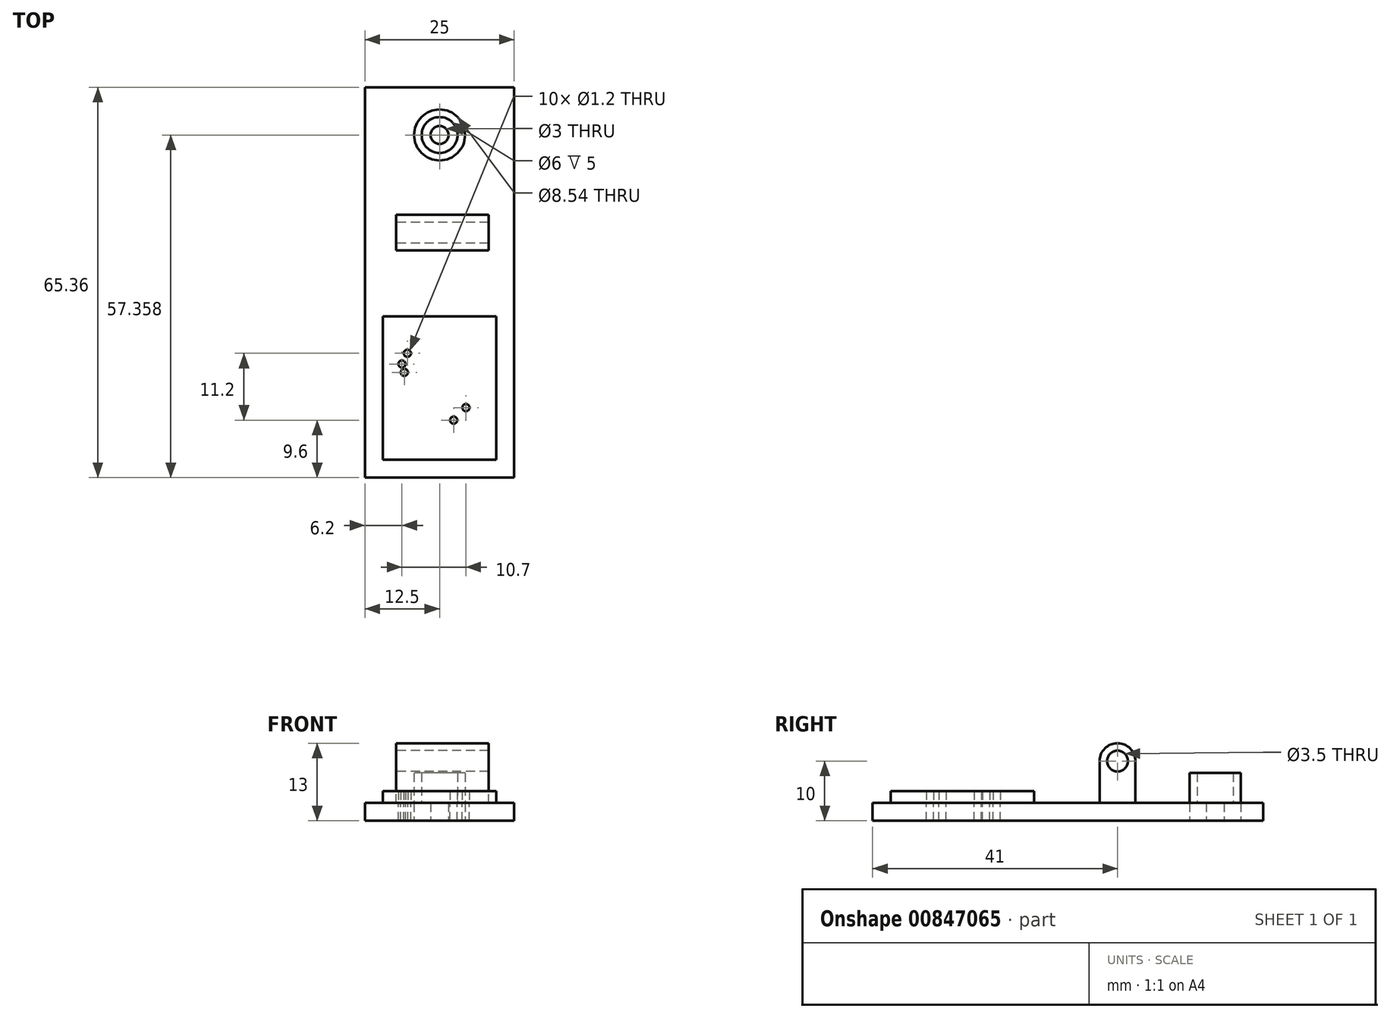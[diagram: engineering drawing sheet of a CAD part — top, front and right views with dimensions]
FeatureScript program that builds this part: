
annotation { "Feature Type Name" : "Feature", "Feature Type Description" : "" }
export const myFeature = defineFeature(function(context is Context, id is Id, definition is map)
    precondition{}
    {
        {
            var Q0;
            Q0=qCreatedBy(makeId("Top.planeOp"),FACE);
            var sketch = newSketch(context, id + "F0", { "sketchPlane" : qUnion([Q0])});
            skLineSegment(sketch, "E0.bottom", {"start": v(0, 0) * mm, "end": v(-19, 0) * mm});
            skLineSegment(sketch, "E0.top", {"start": v(0, 24) * mm, "end": v(-19, 24) * mm});
            skLineSegment(sketch, "E0.left", {"start": v(0, 0) * mm, "end": v(0, 24) * mm});
            skLineSegment(sketch, "E0.right", {"start": v(-19, 0) * mm, "end": v(-19, 24) * mm});
            skLineSegment(sketch, "E1.0", {"start": v(3, 27) * mm, "end": v(-22, 27) * mm});
            skLineSegment(sketch, "E1.1", {"start": v(3, -3) * mm, "end": v(3, 27) * mm});
            skLineSegment(sketch, "E1.2", {"start": v(3, -3) * mm, "end": v(-22, -3) * mm});
            skLineSegment(sketch, "E1.3", {"start": v(-22, -3) * mm, "end": v(-22, 27) * mm});
            skLineSegment(sketch, "E2.bottom", {"start": v(-19, 0) * mm, "end": v(-15.95, 0) * mm});
            skLineSegment(sketch, "E2.top", {"start": v(-19, -3) * mm, "end": v(-15.95, -3) * mm});
            skLineSegment(sketch, "E2.left", {"start": v(-19, 0) * mm, "end": v(-19, -3) * mm});
            skLineSegment(sketch, "E2.right", {"start": v(-15.95, 0) * mm, "end": v(-15.95, -3) * mm});
            skLineSegment(sketch, "E3.bottom", {"start": v(-4.14, 0) * mm, "end": v(0, 0) * mm});
            skLineSegment(sketch, "E3.top", {"start": v(-4.14, -3) * mm, "end": v(0, -3) * mm});
            skLineSegment(sketch, "E3.left", {"start": v(-4.14, 0) * mm, "end": v(-4.14, -3) * mm});
            skLineSegment(sketch, "E3.right", {"start": v(0, 0) * mm, "end": v(0, -3) * mm});
            skLineSegment(sketch, "E4.bottom", {"start": v(-19, 24) * mm, "end": v(0, 24) * mm});
            skLineSegment(sketch, "E4.top", {"start": v(-19, 10.13) * mm, "end": v(0, 10.13) * mm});
            skLineSegment(sketch, "E4.left", {"start": v(-19, 24) * mm, "end": v(-19, 10.13) * mm});
            skLineSegment(sketch, "E4.right", {"start": v(0, 24) * mm, "end": v(0, 10.13) * mm});
            skLineSegment(sketch, "E5.bottom", {"start": v(-10.54, 0) * mm, "end": v(-4.14, 0) * mm});
            skLineSegment(sketch, "E5.top", {"start": v(-10.54, -3) * mm, "end": v(-4.14, -3) * mm});
            skLineSegment(sketch, "E5.left", {"start": v(-10.54, 0) * mm, "end": v(-10.54, -3) * mm});
            skLineSegment(sketch, "E6.bottom", {"start": v(-22, 27) * mm, "end": v(3, 27) * mm});
            skLineSegment(sketch, "E6.top", {"start": v(-22, 62.36) * mm, "end": v(3, 62.36) * mm});
            skLineSegment(sketch, "E6.left", {"start": v(-22, 27) * mm, "end": v(-22, 62.36) * mm});
            skLineSegment(sketch, "E6.right", {"start": v(3, 27) * mm, "end": v(3, 62.36) * mm});
            skCircle(sketch, "E7", {"center": v(-7.14, 6.6) * mm, "radius": 0.6 * mm});
            skCircle(sketch, "E8", {"center": v(-5.1, 8.7) * mm, "radius": 0.6 * mm});
            skCircle(sketch, "E9", {"center": v(-14.9, 17.8) * mm, "radius": 0.6 * mm});
            skCircle(sketch, "E10", {"center": v(-15.8, 16) * mm, "radius": 0.6 * mm});
            skCircle(sketch, "E11", {"center": v(-15.4, 14.6) * mm, "radius": 0.6 * mm});
            skCircle(sketch, "E12", {"center": v(-9.5, 54.36) * mm, "radius": 3 * mm});
            skCircle(sketch, "E13", {"center": v(-9.5, 54.36) * mm, "radius": 4.27 * mm});
            skSolve(sketch);
        }
        {
            var Q0;
            {var subQ1=makeQuery(id+"F0.imprint","IMPRINT",EDGE,{"derivedFrom":sQuery(id+"F0.wireOp",EDGE,"E1.0")});var subQ2=sQuery(id+"F0.wireOp",EDGE,"E2.left");var subQ11=sQuery(id+"F0.wireOp",EDGE,"E0.top");var subQ17=makeQuery(id+"F0.imprint","IMPRINT",EDGE,{"derivedFrom":subQ2});var subQ19=sQuery(id+"F0.wireOp",EDGE,"E3.left");var subQ23=makeQuery(id+"F0.imprint","IMPRINT",EDGE,{"derivedFrom":subQ19});var subQ27=sQuery(id+"F0.wireOp",EDGE,"E2.right");var subQ30=makeQuery(id+"F0.imprint","IMPRINT",EDGE,{"derivedFrom":subQ27});Q0=qUnion([makeQuery(id+"F0.imprint","IMPRINT",FACE,{"disambiguationData":[TD([[subQ30,1.0]])]}),makeQuery(id+"F0.imprint","IMPRINT",FACE,{"disambiguationData":[TD([[subQ1,-1.0]])]}),makeQuery(id+"F0.imprint","IMPRINT",FACE,{"disambiguationData":[TD([[subQ23,1.0]])]}),makeQuery(id+"F0.imprint","IMPRINT",FACE,{"disambiguationData":[TD([[subQ17,1.0]])]}),makeQuery(id+"F0.imprint","IMPRINT",FACE,{"disambiguationData":[TD([[subQ23,-1.0]])]}),makeQuery(id+"F0.imprint","IMPRINT",FACE,{"disambiguationData":[TD([[makeQuery(id+"F0.imprint","IMPRINT",EDGE,{"derivedFrom":subQ11}),-1.0]])]})]);}
            var Q1;
            {var subQ2=sQuery(id+"F0.wireOp",EDGE,"E0.top");Q1=makeQuery(id+"F0.imprint","IMPRINT",FACE,{"disambiguationData":[TD([[makeQuery(id+"F0.imprint","IMPRINT",EDGE,{"derivedFrom":subQ2}),1.0]])]});}
            var Q2;
            {var subQ8=sQuery(id+"F0.wireOp",EDGE,"E4.top");Q2=makeQuery(id+"F0.imprint","IMPRINT",FACE,{"disambiguationData":[TD([[makeQuery(id+"F0.imprint","IMPRINT",EDGE,{"derivedFrom":subQ8}),-1.0]])]});}
            extrude(context, id + "F1", {"entities" : qUnion([Q0, Q1, Q2]), "oppositeDirection" : true, "depth" : 3 * mm, "offsetDistance" : 25 * mm});
        }
        {
            var Q0;
            {var subQ2=sQuery(id+"F0.wireOp",EDGE,"E0.top");Q0=makeQuery(id+"F0.imprint","IMPRINT",FACE,{"disambiguationData":[TD([[makeQuery(id+"F0.imprint","IMPRINT",EDGE,{"derivedFrom":subQ2}),1.0]])]});}
            var Q1;
            {var subQ8=sQuery(id+"F0.wireOp",EDGE,"E4.top");Q1=makeQuery(id+"F0.imprint","IMPRINT",FACE,{"disambiguationData":[TD([[makeQuery(id+"F0.imprint","IMPRINT",EDGE,{"derivedFrom":subQ8}),-1.0]])]});}
            extrude(context, id + "F2", {"entities" : qUnion([Q0, Q1]), "depth" : 2 * mm, "offsetDistance" : 25 * mm});
        }
        {
            var Q0;
            Q0=makeQuery(id+"F0.imprint","IMPRINT",FACE,{"disambiguationData":[TD([[makeQuery(id+"F0.imprint","IMPRINT",EDGE,{"derivedFrom":sQuery(id+"F0.wireOp",EDGE,"E12")}),-1.0]])]});
            extrude(context, id + "F3", {"entities" : qUnion([Q0]), "depth" : 5 * mm, "offsetDistance" : 25 * mm});
        }
        {
            var Q0;
            Q0=makeQuery(id+"F0.imprint","IMPRINT",FACE,{"disambiguationData":[TD([[makeQuery(id+"F0.imprint","IMPRINT",EDGE,{"derivedFrom":sQuery(id+"F0.wireOp",EDGE,"E12")}),1.0]])]});
            var Q1;
            Q1=makeQuery(id+"F0.imprint","IMPRINT",FACE,{"disambiguationData":[TD([[makeQuery(id+"F0.imprint","IMPRINT",EDGE,{"derivedFrom":sQuery(id+"F0.wireOp",EDGE,"E12")}),-1.0]])]});
            extrude(context, id + "F4", {"entities" : qUnion([Q0, Q1]), "oppositeDirection" : true, "depth" : 3 * mm, "offsetDistance" : 25 * mm});
        }
        {
            var Q0;
            Q0=makeQuery(id+"F1.opExtrude","SWEPT_FACE",FACE,{"disambiguationData":[OSD([sQuery(id+"F0.wireOp",EDGE,"E1.3"),sQuery(id+"F0.wireOp",EDGE,"E6.left")])]});
            var sketch = newSketch(context, id + "F5", { "sketchPlane" : qUnion([Q0])});
            skLineSegment(sketch, "E14.bottom", {"start": v(-41, 0) * mm, "end": v(-35, 0) * mm});
            skLineSegment(sketch, "E14.top", {"start": v(-41, 4) * mm, "end": v(-35, 4) * mm});
            skLineSegment(sketch, "E14.left", {"start": v(-41, 0) * mm, "end": v(-41, 4) * mm});
            skLineSegment(sketch, "E14.right", {"start": v(-35, 0) * mm, "end": v(-35, 4) * mm});
            skArc(sketch, "E15", {"start": v(-35, 4) * mm, "mid": v(-38, 7) * mm, "end": v(-41, 4) * mm});
            skCircle(sketch, "E16", {"center": v(-38, 4) * mm, "radius": 1.5 * mm});
            skSolve(sketch);
        }
        {
            var Q0;
            {var subQ2=sQuery(id+"F5.wireOp",EDGE,"E14.bottom");Q0=makeQuery(id+"F5.imprint","IMPRINT",FACE,{"disambiguationData":[TD([[makeQuery(id+"F5.imprint","IMPRINT",EDGE,{"derivedFrom":subQ2}),1.0]])]});}
            cPlane(context, id + "F6", {"entities" : qUnion([Q0]), "cplaneType" : CPlaneType.OFFSET, "offset" : 5.2 * mm, "oppositeDirection" : true, "width" : 150 * mm, "height" : 150 * mm});
        }
        {
            var Q0;
            Q0=qCreatedBy(id+"F6.planeOp",FACE);
            var sketch = newSketch(context, id + "F7", { "sketchPlane" : qUnion([Q0])});
            skLineSegment(sketch, "E17.bottom", {"start": v(-41, 0) * mm, "end": v(-35, 0) * mm});
            skLineSegment(sketch, "E17.top", {"start": v(-41, 7) * mm, "end": v(-35, 7) * mm});
            skLineSegment(sketch, "E17.left", {"start": v(-41, 0) * mm, "end": v(-41, 7) * mm});
            skLineSegment(sketch, "E17.right", {"start": v(-35, 0) * mm, "end": v(-35, 7) * mm});
            skArc(sketch, "E18", {"start": v(-35, 7) * mm, "mid": v(-38, 10) * mm, "end": v(-41, 7) * mm});
            skCircle(sketch, "E19", {"center": v(-38, 7) * mm, "radius": 1.75 * mm});
            skSolve(sketch);
        }
        {
            var Q0;
            {var subQ0=sQuery(id+"F7.wireOp",EDGE,"E18");Q0=makeQuery(id+"F7.imprint","IMPRINT",FACE,{"disambiguationData":[TD([[makeQuery(id+"F7.imprint","IMPRINT",EDGE,{"derivedFrom":subQ0}),1.0]])]});}
            var Q1;
            Q1=makeQuery(id+"F7.imprint","IMPRINT",FACE,{"disambiguationData":[TD([[makeQuery(id+"F7.imprint","IMPRINT",EDGE,{"derivedFrom":sQuery(id+"F7.wireOp",EDGE,"E17.bottom")}),1.0]])]});
            extrude(context, id + "F8", {"entities" : qUnion([Q0, Q1]), "operationType" : NewBodyOperationType.ADD, "oppositeDirection" : true, "depth" : 15.5 * mm, "offsetDistance" : 25 * mm});
        }
        {
            var Q0;
            Q0=makeQuery(id+"F1.opExtrude","CAP_FACE",FACE,{"disambiguationData":[OSD([sQuery(id+"F0.wireOp",EDGE,"E1.1"),sQuery(id+"F0.wireOp",EDGE,"E1.2"),sQuery(id+"F0.wireOp",EDGE,"E1.3"),sQuery(id+"F0.wireOp",EDGE,"E6.top"),sQuery(id+"F0.wireOp",EDGE,"E6.left"),sQuery(id+"F0.wireOp",EDGE,"E6.right"),sQuery(id+"F0.wireOp",EDGE,"E7"),sQuery(id+"F0.wireOp",EDGE,"E8"),sQuery(id+"F0.wireOp",EDGE,"E9"),sQuery(id+"F0.wireOp",EDGE,"E10"),sQuery(id+"F0.wireOp",EDGE,"E11"),sQuery(id+"F0.wireOp",EDGE,"E13")])],"isStart":false});
            var sketch = newSketch(context, id + "F9", { "sketchPlane" : qUnion([Q0])});
            skCircle(sketch, "E20", {"center": v(-9.5, -54.36) * mm, "radius": 1.5 * mm});
            skSolve(sketch);
        }
        {
            var Q0;
            Q0=makeQuery(id+"F9.imprint","IMPRINT",FACE,{"disambiguationData":[TD([[makeQuery(id+"F9.imprint","IMPRINT",EDGE,{"derivedFrom":sQuery(id+"F9.wireOp",EDGE,"E20")}),-1.0]])]});
            extrude(context, id + "F10", {"entities" : qUnion([Q0]), "oppositeDirection" : true, "depth" : 3 * mm, "offsetDistance" : 25 * mm});
        }
    });
